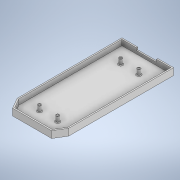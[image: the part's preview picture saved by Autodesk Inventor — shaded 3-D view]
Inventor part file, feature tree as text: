
AUTODESK INVENTOR PART (.ipt)
format: ipt  version: 2022 (Build 260153000, 153)  size: 233,984 bytes
history: native  units: in
note: dims shown in document units (in); Inventor stores cm internally (conversion verified against a paired STEP export)
features: extrude x5, sketch x4, projected_geometry x4, fillet x1
ambient origin geometry x8: Origin, YZ Plane, XZ Plane, XY Plane, X Axis, Y Axis, Z Axis, Center Point
bodies: Solid1 (feature_tree)
feature tree (14):
  sketch  "Sketch1"  dims[d0=0.003in d1=0.0625in]
  extrude  "Extrusion1"  Depth=0.0625in
  extrude  "Extrusion2"  Depth=0.0625in TaperAngle=0.0deg
  extrude  "Extrusion3"  Depth=0.0625in TaperAngle=0.0deg
  extrude  "Extrusion4"  Depth=0.114in
  fillet  "Fillet1"  [1 undecoded]
  extrude  "Extrusion5"  Depth=0.0312in
  sketch  "Sketch2"  dims[d2=0.25in d3=0.0in d4=0.0625in d5=0.0in]
  projected_geometry  "Projected Loop1"
  sketch  "Sketch3"  dims[d6=0.15in d7=0.0625in d8=0.0in]
  projected_geometry  "Projected Loop2"
  projected_geometry  "Projected Loop3"
  projected_geometry  "Projected Loop4"
  sketch  "Sketch5"  dims[d9=0.1in d10=0.1in d11=0.0in d12=0.0312in d13=0.925in d14=0.6705in d15=0.6705in d16=0.114in d17=0.0in]
note: 1 required parameter value undecoded (feature->parameter linkage not recoverable at this tier; creation-order binding heuristic only, values carry confidence <= 0.55)
